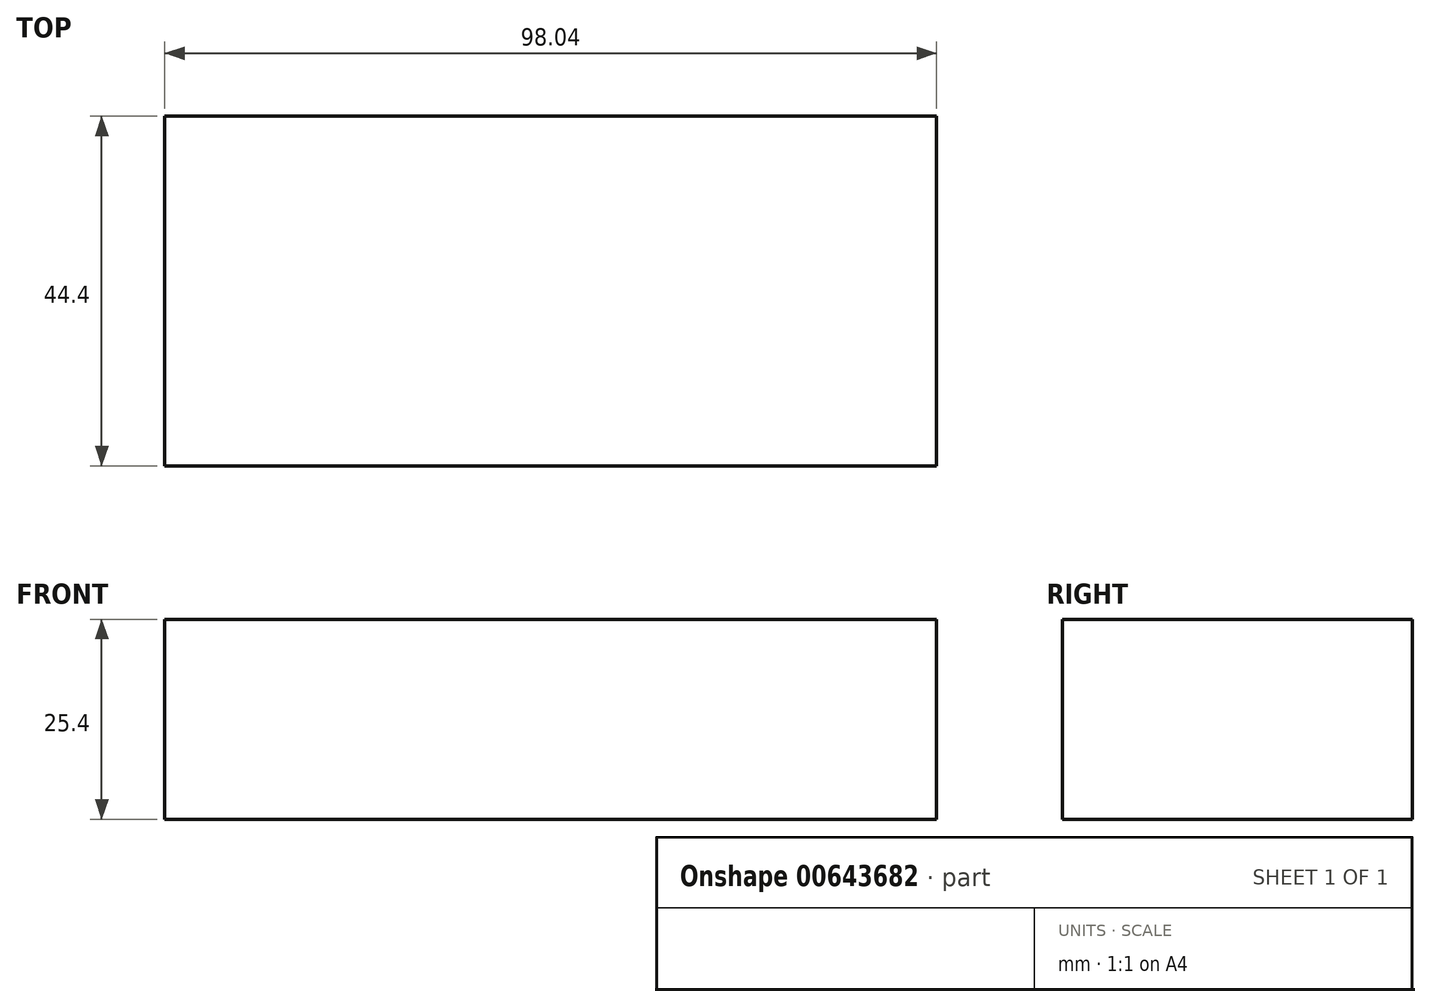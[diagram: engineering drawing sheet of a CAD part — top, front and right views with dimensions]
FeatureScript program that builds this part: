
annotation { "Feature Type Name" : "Feature", "Feature Type Description" : "" }
export const myFeature = defineFeature(function(context is Context, id is Id, definition is map)
    precondition{}
    {
        {
            var Q0;
            Q0=qCreatedBy(makeId("Top.planeOp"),FACE);
            var sketch = newSketch(context, id + "F0", { "sketchPlane" : qUnion([Q0])});
            skLineSegment(sketch, "E0.bottom", {"start": v(-49.02, 22.2) * mm, "end": v(49.02, 22.2) * mm});
            skLineSegment(sketch, "E0.top", {"start": v(-49.02, -22.2) * mm, "end": v(49.02, -22.2) * mm});
            skLineSegment(sketch, "E0.left", {"start": v(-49.02, 22.2) * mm, "end": v(-49.02, -22.2) * mm});
            skLineSegment(sketch, "E0.right", {"start": v(49.02, 22.2) * mm, "end": v(49.02, -22.2) * mm});
            skPoint(sketch, "E0.middle", {"position": v(0, 0) * mm});
            skSolve(sketch);
        }
        {
            var Q0;
            Q0=qSketchRegion(id+"F0",true);
            extrude(context, id + "F1", {"entities" : qUnion([Q0]), "depth" : 25.4 * mm, "offsetDistance" : 25.4 * mm});
        }
    });
